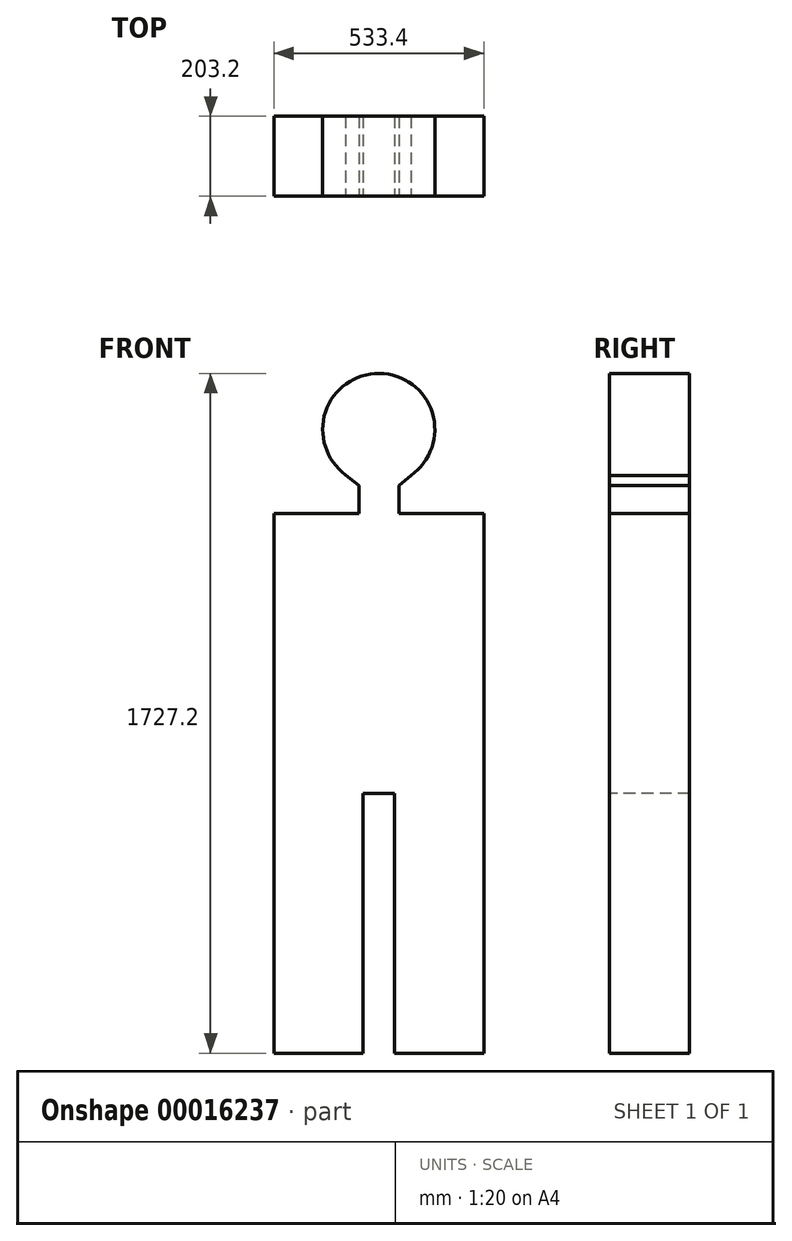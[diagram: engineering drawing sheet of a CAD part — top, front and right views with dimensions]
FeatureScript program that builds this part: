
annotation { "Feature Type Name" : "Feature", "Feature Type Description" : "" }
export const myFeature = defineFeature(function(context is Context, id is Id, definition is map)
    precondition{}
    {
        {
            var Q0;
            Q0=qCreatedBy(makeId("Front.planeOp"),FACE);
            var sketch = newSketch(context, id + "F0", { "sketchPlane" : qUnion([Q0])});
            skLineSegment(sketch, "E0.bottom", {"start": v(-242.43, 1167.4) * mm, "end": v(-26.53, 1167.4) * mm});
            skLineSegment(sketch, "E0.top", {"start": v(-15.17, 456.2) * mm, "end": v(63.7, 456.2) * mm});
            skLineSegment(sketch, "E0.left", {"start": v(-242.43, 1167.4) * mm, "end": v(-242.43, 456.2) * mm});
            skLineSegment(sketch, "E0.right", {"start": v(290.97, 1167.4) * mm, "end": v(290.97, 456.2) * mm});
            skLineSegment(sketch, "E1.top", {"start": v(-242.43, -204.2) * mm, "end": v(-15.17, -204.2) * mm});
            skLineSegment(sketch, "E1.left", {"start": v(-242.43, 456.2) * mm, "end": v(-242.43, -204.2) * mm});
            skLineSegment(sketch, "E1.right", {"start": v(-15.17, 456.2) * mm, "end": v(-15.17, -204.2) * mm});
            skLineSegment(sketch, "E2.top", {"start": v(290.97, -204.2) * mm, "end": v(63.7, -204.2) * mm});
            skLineSegment(sketch, "E2.left", {"start": v(290.97, 456.2) * mm, "end": v(290.97, -204.2) * mm});
            skLineSegment(sketch, "E2.right", {"start": v(63.7, 456.2) * mm, "end": v(63.7, -204.2) * mm});
            skLineSegment(sketch, "E3.left", {"start": v(-26.53, 1167.4) * mm, "end": v(-26.53, 1238) * mm});
            skLineSegment(sketch, "E3.right", {"start": v(75.07, 1167.4) * mm, "end": v(75.07, 1238) * mm});
            skArc(sketch, "E4", {"start": v(105.9, 1263.69) * mm, "mid": v(25.77, 1522.99) * mm, "end": v(-59.8, 1265.43) * mm});
            skLineSegment(sketch, "E5", {"start": v(-26.53, 1238) * mm, "end": v(-59.8, 1265.43) * mm});
            skLineSegment(sketch, "E6", {"start": v(75.07, 1238) * mm, "end": v(105.9, 1263.69) * mm});
            skLineSegment(sketch, "E7.trimOffspring", {"start": v(75.07, 1167.4) * mm, "end": v(290.97, 1167.4) * mm});
            skSolve(sketch);
        }
        {
            var Q0;
            Q0=makeQuery(id+"F0.imprint","IMPRINT",FACE,{"disambiguationData":[TD([[makeQuery(id+"F0.imprint","IMPRINT",EDGE,{"derivedFrom":sQuery(id+"F0.wireOp",EDGE,"E0.bottom")}),-1.0]])]});
            extrude(context, id + "F1", {"entities" : qUnion([Q0]), "oppositeDirection" : true, "depth" : 203.2 * mm});
        }
    });
